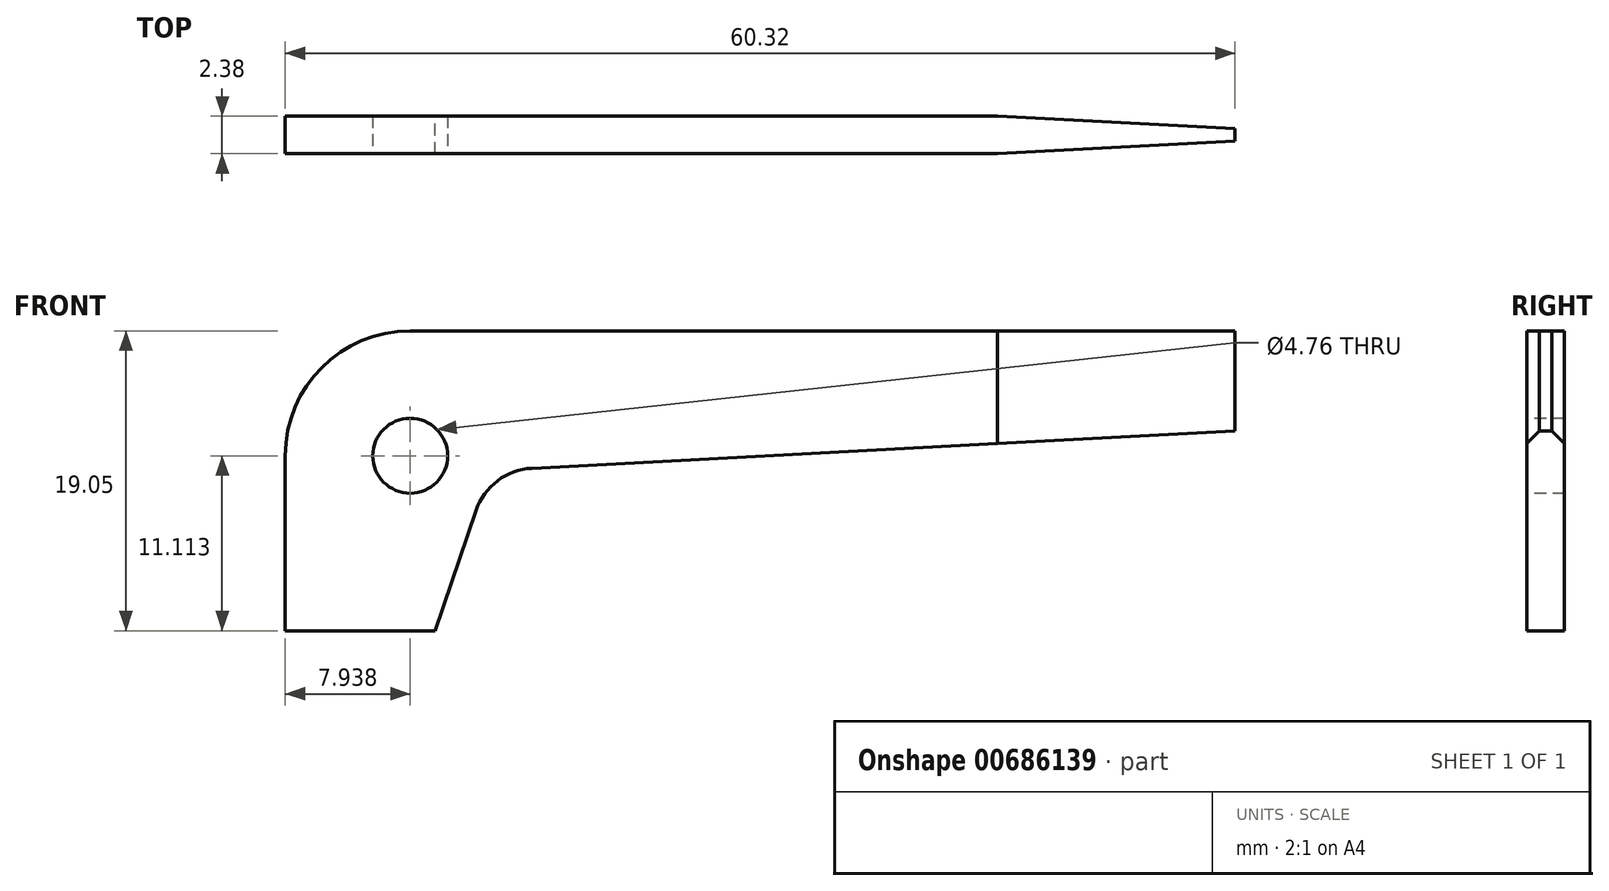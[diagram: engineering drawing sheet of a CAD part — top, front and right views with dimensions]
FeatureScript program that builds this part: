
annotation { "Feature Type Name" : "Feature", "Feature Type Description" : "" }
export const myFeature = defineFeature(function(context is Context, id is Id, definition is map)
    precondition{}
    {
        {
            var Q0;
            Q0=qCreatedBy(makeId("Front.planeOp"),FACE);
            var sketch = newSketch(context, id + "F0", { "sketchPlane" : qUnion([Q0])});
            skLineSegment(sketch, "E0.top", {"start": v(7.94, 19.05) * mm, "end": v(60.32, 19.05) * mm});
            skLineSegment(sketch, "E0.left", {"start": v(0, 0) * mm, "end": v(0, 11.11) * mm});
            skLineSegment(sketch, "E1", {"start": v(9.53, 0) * mm, "end": v(12.11, 7.63) * mm});
            skLineSegment(sketch, "E2", {"start": v(60.33, 12.7) * mm, "end": v(15.66, 10.32) * mm});
            skLineSegment(sketch, "E3", {"start": v(0, 0) * mm, "end": v(9.53, 0) * mm});
            skLineSegment(sketch, "E4", {"start": v(60.33, 19.05) * mm, "end": v(60.33, 12.7) * mm});
            skArc(sketch, "E5", {"start": v(15.66, 10.32) * mm, "mid": v(13.47, 9.52) * mm, "end": v(12.11, 7.63) * mm});
            skPoint(sketch, "E6.visualSharp", {"position": v(0, 19.05) * mm});
            skArc(sketch, "E6.filletArc", {"start": v(7.94, 19.05) * mm, "mid": v(2.32, 16.73) * mm, "end": v(0, 11.11) * mm});
            skSolve(sketch);
        }
        {
            var Q0;
            Q0 = qSketchRegion(id + "F0", true);
            extrude(context, id + "F1", {"entities" : qUnion([Q0]), "depth" : 2.38 * mm, "offsetDistance" : 25.4 * mm});
        }
        {
            var Q0;
            Q0=makeQuery(id+"F1.opExtrude","CAP_FACE",FACE,{"disambiguationData":[OSD([sQuery(id+"F0.wireOp",EDGE,"E0.top"),sQuery(id+"F0.wireOp",EDGE,"E0.left"),sQuery(id+"F0.wireOp",EDGE,"E1"),sQuery(id+"F0.wireOp",EDGE,"E2"),sQuery(id+"F0.wireOp",EDGE,"E3"),sQuery(id+"F0.wireOp",EDGE,"E4"),sQuery(id+"F0.wireOp",EDGE,"E5"),sQuery(id+"F0.wireOp",EDGE,"E6.filletArc")])],"isStart":false});
            var sketch = newSketch(context, id + "F2", { "sketchPlane" : qUnion([Q0])});
            skCircle(sketch, "E7", {"center": v(7.94, 11.11) * mm, "radius": 2.38 * mm});
            skSolve(sketch);
        }
        {
            var Q0;
            Q0=makeQuery(id+"F2.imprint","IMPRINT",FACE,{"disambiguationData":[TD([[makeQuery(id+"F2.imprint","IMPRINT",EDGE,{"derivedFrom":sQuery(id+"F2.wireOp",EDGE,"E7")}),1.0]])]});
            extrude(context, id + "F3", {"entities" : qUnion([Q0]), "operationType" : NewBodyOperationType.REMOVE, "oppositeDirection" : true, "depth" : 25.4 * mm, "offsetDistance" : 25.4 * mm});
        }
        {
            var Q0;
            Q0=makeQuery(id+"F1.opExtrude","SWEPT_FACE",FACE,{"disambiguationData":[OSD([sQuery(id+"F0.wireOp",EDGE,"E0.top")])]});
            var sketch = newSketch(context, id + "F4", { "sketchPlane" : qUnion([Q0])});
            skLineSegment(sketch, "E8", {"start": v(45.24, 0) * mm, "end": v(60.32, -0.8) * mm});
            skLineSegment(sketch, "E9", {"start": v(45.24, 0) * mm, "end": v(60.32, 0) * mm});
            skLineSegment(sketch, "E10", {"start": v(60.32, 0) * mm, "end": v(60.32, -0.8) * mm});
            skLineSegment(sketch, "E11.MirrorCS", {"start": v(45.24, -2.38) * mm, "end": v(60.32, -1.59) * mm});
            skLineSegment(sketch, "E12.MirrorCS", {"start": v(45.24, -2.38) * mm, "end": v(60.32, -2.38) * mm});
            skLineSegment(sketch, "E13.MirrorCS", {"start": v(60.32, -2.38) * mm, "end": v(60.32, -1.59) * mm});
            skSolve(sketch);
        }
        {
            var Q0;
            Q0=makeQuery(id+"F4.imprint","IMPRINT",FACE,{"disambiguationData":[TD([[makeQuery(id+"F4.imprint","IMPRINT",EDGE,{"derivedFrom":sQuery(id+"F4.wireOp",EDGE,"E8")}),1.0]])]});
            var Q1;
            Q1=makeQuery(id+"F4.imprint","IMPRINT",FACE,{"disambiguationData":[TD([[makeQuery(id+"F4.imprint","IMPRINT",EDGE,{"derivedFrom":sQuery(id+"F4.wireOp",EDGE,"E11.MirrorCS")}),-1.0]])]});
            extrude(context, id + "F5", {"entities" : qUnion([Q0, Q1]), "operationType" : NewBodyOperationType.REMOVE, "oppositeDirection" : true, "depth" : 25.4 * mm, "offsetDistance" : 25.4 * mm});
        }
    });
